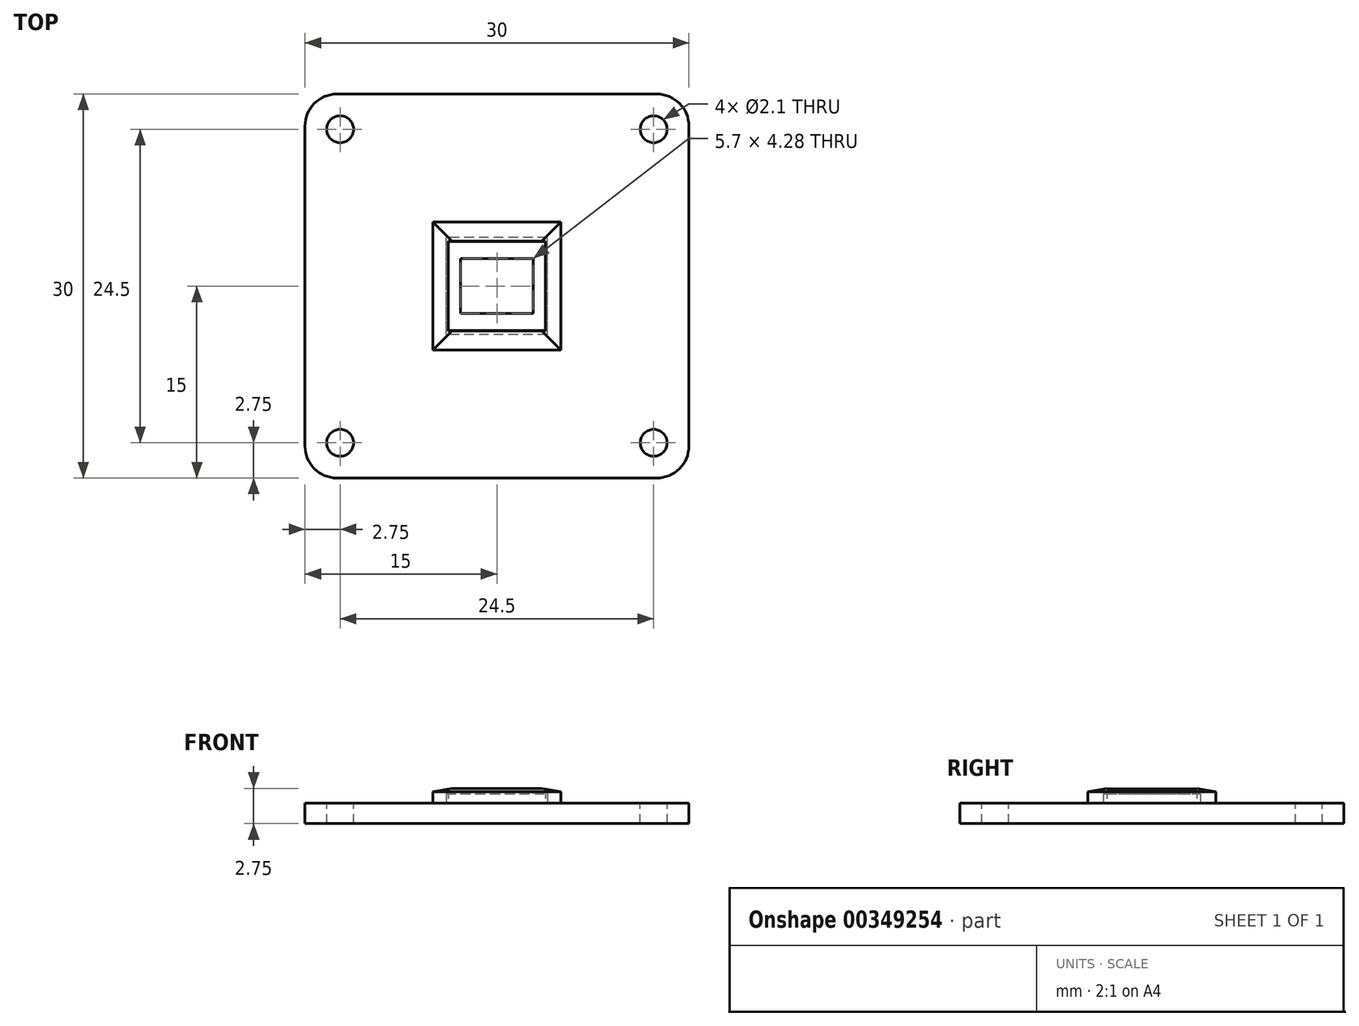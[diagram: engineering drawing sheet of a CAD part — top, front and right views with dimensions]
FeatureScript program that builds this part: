
annotation { "Feature Type Name" : "Feature", "Feature Type Description" : "" }
export const myFeature = defineFeature(function(context is Context, id is Id, definition is map)
    precondition{}
    {
        {
            var Q0;
            Q0=qCreatedBy(makeId("Top.planeOp"),FACE);
            var sketch = newSketch(context, id + "F0", { "sketchPlane" : qUnion([Q0])});
            skLineSegment(sketch, "E0.bottom", {"start": v(-12.5, 15) * mm, "end": v(12.5, 15) * mm});
            skLineSegment(sketch, "E0.top", {"start": v(-12.5, -15) * mm, "end": v(12.5, -15) * mm});
            skLineSegment(sketch, "E0.left", {"start": v(-15, 12.5) * mm, "end": v(-15, -12.5) * mm});
            skLineSegment(sketch, "E0.right", {"start": v(15, 12.5) * mm, "end": v(15, -12.5) * mm});
            skPoint(sketch, "E0.middle", {"position": v(0, 0) * mm});
            skPoint(sketch, "E1.visualSharp", {"position": v(-15, 15) * mm});
            skArc(sketch, "E1.filletArc", {"start": v(-12.5, 15) * mm, "mid": v(-14.27, 14.27) * mm, "end": v(-15, 12.5) * mm});
            skPoint(sketch, "E2.visualSharp", {"position": v(15, 15) * mm});
            skArc(sketch, "E2.filletArc", {"start": v(15, 12.5) * mm, "mid": v(14.27, 14.27) * mm, "end": v(12.5, 15) * mm});
            skPoint(sketch, "E3.visualSharp", {"position": v(15, -15) * mm});
            skArc(sketch, "E3.filletArc", {"start": v(12.5, -15) * mm, "mid": v(14.27, -14.27) * mm, "end": v(15, -12.5) * mm});
            skPoint(sketch, "E4.visualSharp", {"position": v(-15, -15) * mm});
            skArc(sketch, "E4.filletArc", {"start": v(-15, -12.5) * mm, "mid": v(-14.27, -14.27) * mm, "end": v(-12.5, -15) * mm});
            skSolve(sketch);
        }
        {
            var Q0;
            Q0=qSketchRegion(id+"F0",true);
            extrude(context, id + "F1", {"entities" : qUnion([Q0]), "oppositeDirection" : true, "depth" : 1.59 * mm});
        }
        {
            var Q0;
            Q0=makeQuery(id+"F1.opExtrude","CAP_FACE",FACE,{"disambiguationData":[OSD([sQuery(id+"F0.wireOp",EDGE,"E0.bottom"),sQuery(id+"F0.wireOp",EDGE,"E0.top"),sQuery(id+"F0.wireOp",EDGE,"E0.left"),sQuery(id+"F0.wireOp",EDGE,"E0.right"),sQuery(id+"F0.wireOp",EDGE,"E1.filletArc"),sQuery(id+"F0.wireOp",EDGE,"E2.filletArc"),sQuery(id+"F0.wireOp",EDGE,"E3.filletArc"),sQuery(id+"F0.wireOp",EDGE,"E4.filletArc")])],"isStart":true});
            var sketch = newSketch(context, id + "F2", { "sketchPlane" : qUnion([Q0])});
            skLineSegment(sketch, "E5.bottom", {"start": v(12.25, -12.25) * mm, "end": v(-12.25, -12.25) * mm, "construction": true});
            skLineSegment(sketch, "E5.top", {"start": v(12.25, 12.25) * mm, "end": v(-12.25, 12.25) * mm, "construction": true});
            skLineSegment(sketch, "E5.left", {"start": v(12.25, -12.25) * mm, "end": v(12.25, 12.25) * mm, "construction": true});
            skLineSegment(sketch, "E5.right", {"start": v(-12.25, -12.25) * mm, "end": v(-12.25, 12.25) * mm, "construction": true});
            skPoint(sketch, "E5.middle", {"position": v(0, 0) * mm});
            skCircle(sketch, "E6", {"center": v(-12.25, 12.25) * mm, "radius": 1.05 * mm});
            skCircle(sketch, "E7", {"center": v(12.25, 12.25) * mm, "radius": 1.05 * mm});
            skCircle(sketch, "E8", {"center": v(12.25, -12.25) * mm, "radius": 1.05 * mm});
            skCircle(sketch, "E9", {"center": v(-12.25, -12.25) * mm, "radius": 1.05 * mm});
            skSolve(sketch);
        }
        {
            var Q0;
            Q0=qSketchRegion(id+"F2",true);
            extrude(context, id + "F3", {"entities" : qUnion([Q0]), "operationType" : NewBodyOperationType.REMOVE, "endBound" : BoundingType.THROUGH_ALL, "oppositeDirection" : true, "depth" : 25 * mm});
        }
        {
            var Q0;
            Q0=makeQuery(id+"F1.opExtrude","CAP_FACE",FACE,{"disambiguationData":[OSD([sQuery(id+"F0.wireOp",EDGE,"E0.bottom"),sQuery(id+"F0.wireOp",EDGE,"E0.top"),sQuery(id+"F0.wireOp",EDGE,"E0.left"),sQuery(id+"F0.wireOp",EDGE,"E0.right"),sQuery(id+"F0.wireOp",EDGE,"E1.filletArc"),sQuery(id+"F0.wireOp",EDGE,"E2.filletArc"),sQuery(id+"F0.wireOp",EDGE,"E3.filletArc"),sQuery(id+"F0.wireOp",EDGE,"E4.filletArc")])],"isStart":true});
            var sketch = newSketch(context, id + "F4", { "sketchPlane" : qUnion([Q0])});
            skLineSegment(sketch, "E10.bottom", {"start": v(-5, 5) * mm, "end": v(5, 5) * mm});
            skLineSegment(sketch, "E10.top", {"start": v(-5, -5) * mm, "end": v(5, -5) * mm});
            skLineSegment(sketch, "E10.left", {"start": v(-5, 5) * mm, "end": v(-5, -5) * mm});
            skLineSegment(sketch, "E10.right", {"start": v(5, 5) * mm, "end": v(5, -5) * mm});
            skPoint(sketch, "E10.middle", {"position": v(0, 0) * mm});
            skLineSegment(sketch, "E11.bottom", {"start": v(-3.78, 3.5) * mm, "end": v(3.79, 3.5) * mm});
            skLineSegment(sketch, "E11.top", {"start": v(-3.79, -3.5) * mm, "end": v(3.78, -3.5) * mm});
            skLineSegment(sketch, "E11.left", {"start": v(-3.78, 3.5) * mm, "end": v(-3.79, -3.51) * mm});
            skLineSegment(sketch, "E11.right", {"start": v(3.79, 3.5) * mm, "end": v(3.78, -3.51) * mm});
            skSolve(sketch);
        }
        {
            var Q0;
            Q0=qSketchRegion(id+"F4",true);
            extrude(context, id + "F5", {"entities" : qUnion([Q0]), "depth" : 1.25 * mm});
        }
        {
            var Q0;
            Q0=makeQuery(id+"F5.opExtrude","CAP_EDGE",EDGE,{"disambiguationData":[OSD([sQuery(id+"F4.wireOp",EDGE,"E10.top")])],"isStart":false});
            var Q1;
            Q1=makeQuery(id+"F5.opExtrude","CAP_EDGE",EDGE,{"disambiguationData":[OSD([sQuery(id+"F4.wireOp",EDGE,"E10.bottom")])],"isStart":false});
            var Q2;
            Q2=makeQuery(id+"F5.opExtrude","CAP_EDGE",EDGE,{"disambiguationData":[OSD([sQuery(id+"F4.wireOp",EDGE,"E10.right")])],"isStart":false});
            var Q3;
            Q3=makeQuery(id+"F5.opExtrude","CAP_EDGE",EDGE,{"disambiguationData":[OSD([sQuery(id+"F4.wireOp",EDGE,"E10.left")])],"isStart":false});
            chamfer(context, id + "F6", {"entities" : qUnion([Q0, Q1, Q2, Q3]), "chamferType" : ChamferType.OFFSET_ANGLE, "width" : 2 * mm, "oppositeDirection" : false, "angle" : 10 * degree, "tangentPropagation" : true});
        }
        {
            var Q0;
            Q0=makeQuery(id+"F1.opExtrude","CAP_FACE",FACE,{"disambiguationData":[OSD([sQuery(id+"F0.wireOp",EDGE,"E0.bottom"),sQuery(id+"F0.wireOp",EDGE,"E0.top"),sQuery(id+"F0.wireOp",EDGE,"E0.left"),sQuery(id+"F0.wireOp",EDGE,"E0.right"),sQuery(id+"F0.wireOp",EDGE,"E1.filletArc"),sQuery(id+"F0.wireOp",EDGE,"E2.filletArc"),sQuery(id+"F0.wireOp",EDGE,"E3.filletArc"),sQuery(id+"F0.wireOp",EDGE,"E4.filletArc")])],"isStart":true});
            var sketch = newSketch(context, id + "F7", { "sketchPlane" : qUnion([Q0])});
            skLineSegment(sketch, "E12.bottom", {"start": v(3.95, -3.8) * mm, "end": v(-3.95, -3.8) * mm});
            skLineSegment(sketch, "E12.top", {"start": v(3.95, 3.8) * mm, "end": v(-3.95, 3.8) * mm});
            skLineSegment(sketch, "E12.left", {"start": v(3.95, -3.8) * mm, "end": v(3.95, 3.8) * mm});
            skLineSegment(sketch, "E12.right", {"start": v(-3.95, -3.8) * mm, "end": v(-3.95, 3.8) * mm});
            skPoint(sketch, "E12.middle", {"position": v(0, 0) * mm});
            skSolve(sketch);
        }
        {
            var Q0;
            Q0=qSketchRegion(id+"F7",true);
            extrude(context, id + "F8", {"entities" : qUnion([Q0]), "depth" : .725 * mm});
        }
        {
            var Q0;
            Q0=makeQuery(id+"F8.opExtrude","CAP_FACE",FACE,{"disambiguationData":[OSD([sQuery(id+"F7.wireOp",EDGE,"E12.bottom"),sQuery(id+"F7.wireOp",EDGE,"E12.top"),sQuery(id+"F7.wireOp",EDGE,"E12.left"),sQuery(id+"F7.wireOp",EDGE,"E12.right")])],"isStart":false});
            var sketch = newSketch(context, id + "F9", { "sketchPlane" : qUnion([Q0])});
            skLineSegment(sketch, "E13.bottom", {"start": v(-3.95, 3.47) * mm, "end": v(3.95, 3.47) * mm});
            skLineSegment(sketch, "E13.top", {"start": v(-3.95, -3.47) * mm, "end": v(3.95, -3.47) * mm});
            skLineSegment(sketch, "E13.left", {"start": v(-3.95, 3.47) * mm, "end": v(-3.95, -3.47) * mm});
            skLineSegment(sketch, "E13.right", {"start": v(3.95, 3.47) * mm, "end": v(3.95, -3.47) * mm});
            skPoint(sketch, "E13.middle", {"position": v(0, 0) * mm});
            skLineSegment(sketch, "E14.bottom", {"start": v(-2.85, 2.14) * mm, "end": v(2.85, 2.14) * mm});
            skLineSegment(sketch, "E14.top", {"start": v(-2.85, -2.14) * mm, "end": v(2.85, -2.14) * mm});
            skLineSegment(sketch, "E14.left", {"start": v(-2.85, 2.14) * mm, "end": v(-2.85, -2.14) * mm});
            skLineSegment(sketch, "E14.right", {"start": v(2.85, 2.14) * mm, "end": v(2.85, -2.14) * mm});
            skSolve(sketch);
        }
        {
            var Q0;
            Q0=qSketchRegion(id+"F9",true);
            extrude(context, id + "F10", {"entities" : qUnion([Q0]), "depth" : .1 * mm});
        }
    });
